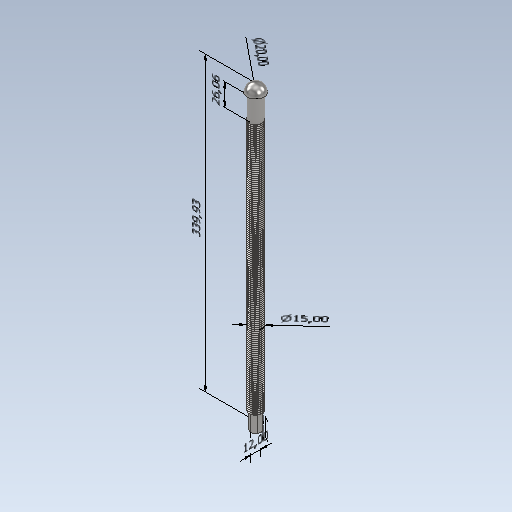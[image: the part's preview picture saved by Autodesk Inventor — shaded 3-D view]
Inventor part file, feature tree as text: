
AUTODESK INVENTOR PART (.ipt)
format: ipt  version: 2021 (Build 250183000, 183)  size: 3,040,768 bytes
history: native  units: mm
features: sketch x11, other x7, extrude x7, thicken_offset x7, revolve x2, helix x2
ambient origin geometry x8: Origin, YZ Plane, XZ Plane, XY Plane, X Axis, Y Axis, Z Axis, Center Point
bodies: Solid1 (feature_tree)
feature tree (36):
  other  "Annotations"
  extrude  "Extrusion1"  Depth=350.0mm TaperAngle=0.0deg
  revolve  "Revolution1"  [1 undecoded]
  extrude  "Extrusion2"  Depth=20.0mm TaperAngle=0.0deg
  extrude  "Extrusion3"  Depth=10.0mm
  revolve  "Revolution2"  Angle=90.0deg
  thicken_offset  "Thicken1"
  thicken_offset  "Thicken2"
  thicken_offset  "Thicken3"
  thicken_offset  "Thicken4"
  thicken_offset  "Thicken5"
  thicken_offset  "Thicken6"
  thicken_offset  "Thicken7"
  helix  "Coil1"  [1 undecoded]
  extrude  "Extrusion4"  Depth=10.0mm
  extrude  "Extrusion5"  Depth=10.0mm
  helix  "Coil2"  [1 undecoded]
  extrude  "Extrusion6"  Depth=10.0mm
  extrude  "Extrusion7"  Depth=10.0mm
  sketch  "Sketch1"  dims[d0=15.0mm d1=350.0mm d2=0.0mm]
  sketch  "Sketch2"  dims[d3=15.0mm d4=9.0mm]
  sketch  "Sketch3"  dims[d5=90.0deg d6=20.0mm d7=0.0mm]
  sketch  "Sketch4"  dims[d14=30.0mm d15=0.0mm d16=10.0mm]
  sketch  "Sketch5"  dims[d17=20.0mm d18=90.0deg d19=10.0mm]
  sketch  "Sketch6"  dims[d20=10.0mm d21=10.0mm]
  sketch  "Sketch7"  dims[d22=10.0mm d23=10.0mm d24=10.0mm]
  sketch  "Sketch8"  dims[d25=10.0mm d26=10.0mm]
  sketch  "Sketch9"  dims[d27=10.0mm d28=10.0mm]
  sketch  "Sketch10"  dims[d29=10.0mm]
  sketch  "Sketch11"  dims[d30=10.0mm d31=10.0mm d32=10.0mm d36=20.0mm d38=1.22686mm d39=2.0mm d40=0.28868mm d41=1.0mm d46=2.0mm d47=10.0mm d48=1570.0mm d49=0.0mm d50=90.0deg d51=90.0deg d52=0.0mm d53=0.0mm d54=15.0mm d55=340.0mm d56=0.0mm d57=20.0mm d58=0.0mm d60=1.22686mm d61=0.28868mm d62=60.0deg d63=60.0deg d64=2.0mm d65=10.0mm d66=1570.0mm d67=0.0mm d68=90.0deg d69=90.0deg d70=0.0mm d71=0.0mm d72=15.0mm d73=20.0mm d74=0.0mm d75=6.0mm d76=20.0mm d77=0.0mm d10=7.805911mm d11=15.0mm d78=9.484691mm d79=4.612622mm d8=40.227195mm d80=339.934981mm d81=0.0mm d82=10.0mm d83=20.0mm d84=26.060409mm d85=39.531131mm d86=20.0mm d87=12.0mm d9=2.677461mm]
  other  "Diameter Dimension 1"
  other  "Linear Dimension 1"
  other  "Linear Dimension 2"
  other  "Linear Dimension 3"
  other  "Diameter Dimension 2"
  other  "Linear Dimension 4"
note: 3 required parameter values undecoded (feature->parameter linkage not recoverable at this tier; creation-order binding heuristic only, values carry confidence <= 0.55)